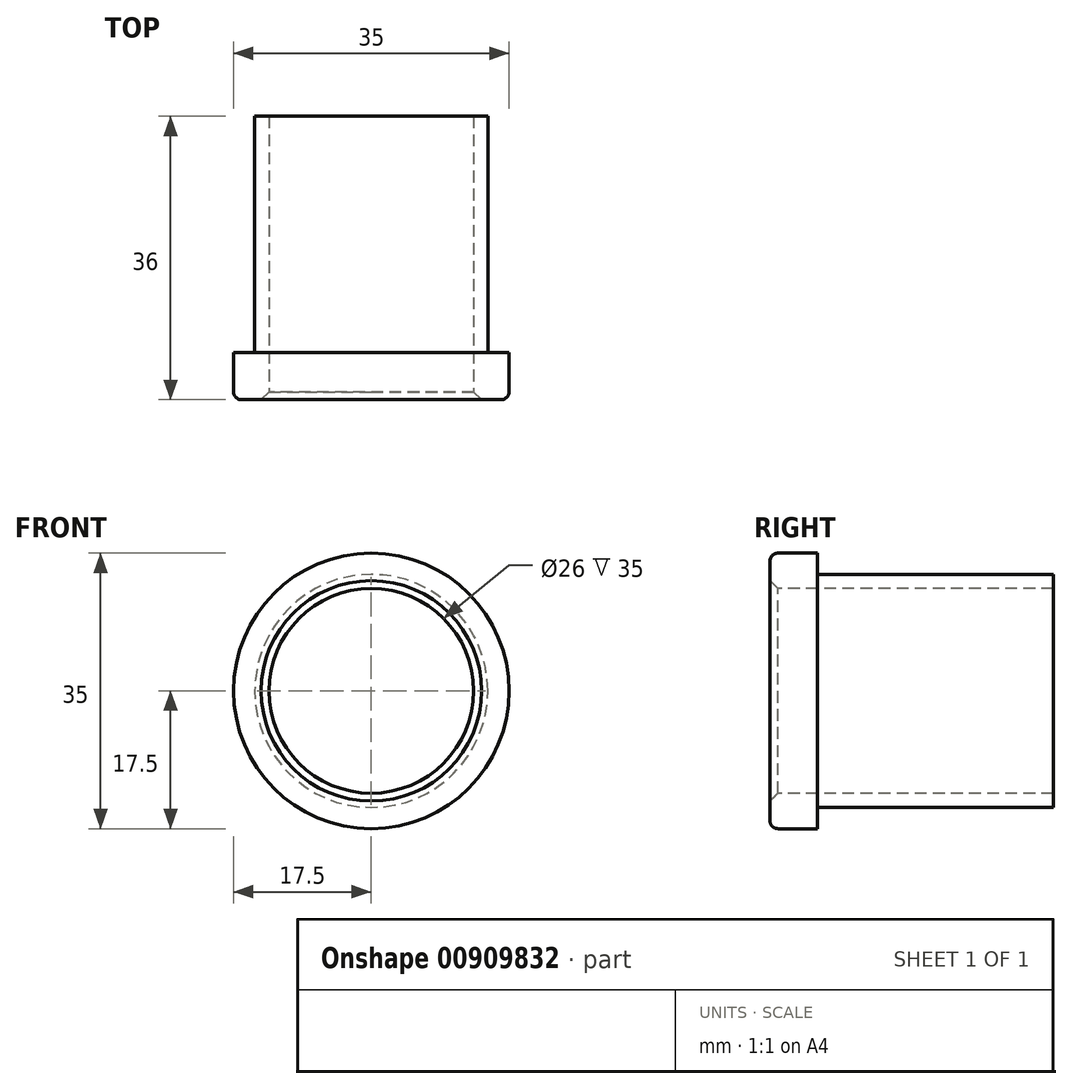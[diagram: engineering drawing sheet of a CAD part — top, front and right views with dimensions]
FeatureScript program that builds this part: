
annotation { "Feature Type Name" : "Feature", "Feature Type Description" : "" }
export const myFeature = defineFeature(function(context is Context, id is Id, definition is map)
    precondition{}
    {
        {
            var Q0;
            Q0=qCreatedBy(makeId("Front.planeOp"),FACE);
            var sketch = newSketch(context, id + "F0", { "sketchPlane" : qUnion([Q0])});
            skCircle(sketch, "E0", {"center": v(0, 0) * mm, "radius": 17.5 * mm});
            skSolve(sketch);
        }
        {
            var Q0;
            Q0=makeQuery(id+"F0.imprint","IMPRINT",FACE,{"disambiguationData":[TD([[makeQuery(id+"F0.imprint","IMPRINT",EDGE,{"derivedFrom":sQuery(id+"F0.wireOp",EDGE,"E0")}),1.0]])]});
            extrude(context, id + "F1", {"entities" : qUnion([Q0]), "depth" : 6 * mm, "offsetDistance" : 25 * mm});
        }
        {
            var Q0;
            Q0=makeQuery(id+"F1.opExtrude","CAP_EDGE",EDGE,{"disambiguationData":[OSD([sQuery(id+"F0.wireOp",EDGE,"E0")])],"isStart":false});
            fillet(context, id + "F2", {"entities" : qUnion([Q0]), "radius" : 1 * mm, "tangentPropagation" : true, "allowEdgeOverflow" : false});
        }
        {
            var Q0;
            Q0=makeQuery(id+"F1.opExtrude","CAP_FACE",FACE,{"disambiguationData":[OSD([sQuery(id+"F0.wireOp",EDGE,"E0")])],"isStart":true});
            var sketch = newSketch(context, id + "F3", { "sketchPlane" : qUnion([Q0])});
            skPoint(sketch, "E1", {"position": v(0, 0) * mm});
            skCircle(sketch, "E2", {"center": v(0, 0) * mm, "radius": 14.8 * mm});
            skSolve(sketch);
        }
        {
            var Q0;
            Q0=makeQuery(id+"F3.imprint","IMPRINT",FACE,{"disambiguationData":[TD([[makeQuery(id+"F3.imprint","IMPRINT",EDGE,{"derivedFrom":sQuery(id+"F3.wireOp",EDGE,"E2")}),1.0]])]});
            extrude(context, id + "F4", {"entities" : qUnion([Q0]), "operationType" : NewBodyOperationType.ADD, "depth" : 30 * mm, "offsetDistance" : 25 * mm});
        }
        {
            var Q0;
            Q0=makeQuery(id+"F1.opExtrude","CAP_FACE",FACE,{"disambiguationData":[OSD([sQuery(id+"F0.wireOp",EDGE,"E0")])],"isStart":false});
            var sketch = newSketch(context, id + "F5", { "sketchPlane" : qUnion([Q0])});
            skPoint(sketch, "E3", {"position": v(0, 0) * mm});
            skSolve(sketch);
        }
        {
            var Q0;
            Q0=sQuery(id+"F5.wireOp",VERTEX,"E3");
            var Q1;
            Q1=makeQuery(id+"F1.opExtrude","SWEPT_BODY",BODY,{"disambiguationData":[OSD([sQuery(id+"F0.wireOp",EDGE,"E0")])]});
            hole(context, id + "F6", {"style" : HoleStyle.C_SINK, "endStyle" : HoleEndStyle.BLIND, "holeDiameter" : 26 * mm, "cSinkDiameter" : 28 * mm, "cSinkAngle" : 90 * degree, "majorDiameter" : 5 * mm, "holeDepth" : 60 * mm, "isTappedThrough" : true, "tappedDepth" : 12 * mm, "tapClearance" : 3, "startFromSketch" : true, "locations" : qUnion([Q0]), "scope" : qUnion([Q1])});
        }
    });
